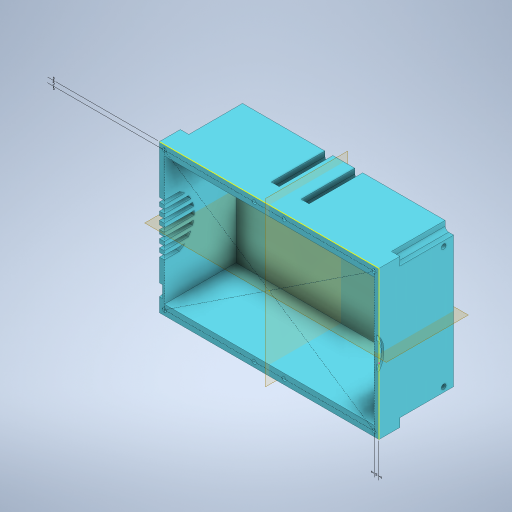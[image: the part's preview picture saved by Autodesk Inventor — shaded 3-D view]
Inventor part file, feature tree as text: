
AUTODESK INVENTOR PART (.ipt)
format: ipt  version: 2023 (Build 270158030, 158C)  size: 828,416 bytes
history: native  units: mm
features: sketch x15, extrude x14, mirror x4, hole x2, emboss x1, projected_geometry x1
ambient origin geometry x8: Origin, YZ Plane, XZ Plane, XY Plane, X Axis, Y Axis, Z Axis, Center Point
bodies: Solid1 (feature_tree)
feature tree (37):
  extrude  "MainInnerBodyExtrusion"  Depth=220.7mm
  extrude  "HoleForCamerabase"  Depth=15.7mm
  extrude  "HoleForFan"  Depth=52.0mm
  extrude  "SlotsForRearFan"  TaperAngle=0.0deg  [1 undecoded]
  sketch  "Sketch23"  dims[d8=47.0mm d9=0.0mm]
  hole  "Screw hole for 6-32 screw"  [1 undecoded]
  extrude  "Extrusion19"  Depth=47.0mm
  extrude  "Extrusion21"  Depth=60.0mm
  extrude  "Extrusion22"  Depth=4.0mm
  hole  "Hole5"  [1 undecoded]
  sketch  "Sketch31"  dims[d69=2.0mm d71=4.0mm]
  extrude  "Extrusion24"  Depth=10.0mm TaperAngle=0.0deg
  mirror  "Mirror2"
  mirror  "Mirror3"
  extrude  "Extrusion25"  Depth=15.0mm
  mirror  "Mirror4"
  mirror  "Mirror5"
  sketch  "Sketch33"  dims[d72=4.0mm d73=4.0mm]
  emboss  "Emboss1"
  extrude  "HolesForFilter"  Depth=5.0mm
  extrude  "Extrusion27"  Depth=30.0mm
  extrude  "Extrusion28"  Depth=12.0mm
  extrude  "Extrusion30"  Depth=7.0mm
  extrude  "Extrusion31"  Depth=40.0mm TaperAngle=0.0deg
  sketch  "Sketch1"  dims[d0=220.7mm d1=149.0mm]
  sketch  "Sketch3"  dims[d2=75.0mm d3=0.0mm d5=15.7mm]
  sketch  "Sketch4"  dims[d6=52.0mm d7=57.0mm]
  sketch  "Sketch26"  dims[d13=16.0mm d14=62.0mm]
  sketch  "Sketch28"  dims[d15=3.0mm d16=47.0mm]
  sketch  "Sketch29"  dims[d17=0.0mm d67=60.0mm]
  sketch  "Sketch34"  dims[d75=4.0mm d76=10.0mm d77=0.0mm]
  sketch  "Sketch35"  dims[d79=22.0mm d95=15.0mm]
  sketch  "Sketch36"  dims[d106=5.0mm d108=5.0mm]
  sketch  "Sketch37"  dims[d116=4.051mm d117=6.0mm d118=12.7mm d119=2.362mm d120=90.0deg d121=15.0mm d122=20.594885mm d142=30.0mm]
  sketch  "Sketch39"  dims[d143=20.0mm d144=12.0mm]
  projected_geometry  "Projected Loop3"
  sketch  "Sketch40"  dims[d145=10.0mm d146=0.0mm d150=7.0mm d151=58.0mm d152=0.0mm d153=10.0mm d154=5.0mm d155=72.0mm d156=0.0mm d157=30.0mm d158=4.051mm d159=6.0mm d160=8.0mm d161=58.0mm d162=14.3117mm d163=8.0mm d164=20.594885mm d167=54.0mm d168=0.0mm d169=54.0mm d170=0.0mm d178=25.4mm d179=1.0mm d180=0.0mm d181=140.0mm d182=52.25mm d183=21.0mm d184=47.0mm d185=2.25mm d186=0.0mm d187=3.0mm d188=20.0mm d189=1.5mm d190=1.5mm d191=7.0mm d192=0.0mm d193=4.8514mm d194=5.0mm d195=10.0mm d196=10.0mm d197=5.0mm d198=9.525mm d199=0.0mm d203=40.0mm d204=2.0mm d205=0.0mm d206=2.0mm d207=0.0mm]
note: 3 required parameter values undecoded (feature->parameter linkage not recoverable at this tier; creation-order binding heuristic only, values carry confidence <= 0.55)
